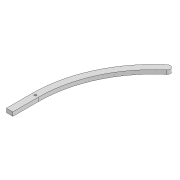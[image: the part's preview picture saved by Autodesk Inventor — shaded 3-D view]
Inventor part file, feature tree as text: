
AUTODESK INVENTOR PART (.ipt)
format: ipt  version: 2022 (Build 260153000, 153)  size: 93,696 bytes
history: native  units: mm
features: extrude x1, sketch x1
ambient origin geometry x8: Origin, YZ Plane, XZ Plane, XY Plane, X Axis, Y Axis, Z Axis, Center Point
bodies: Solid1 (feature_tree)
feature tree (2):
  extrude  "Extrusion1"  Depth=10.0mm
  sketch  "Sketch1"  dims[d0=10.0mm d1=10.0mm d3=40.0mm d4=10.0mm d6=180.0mm d7=60.0mm d8=3.3mm d9=6.0mm d10=0.0mm]
